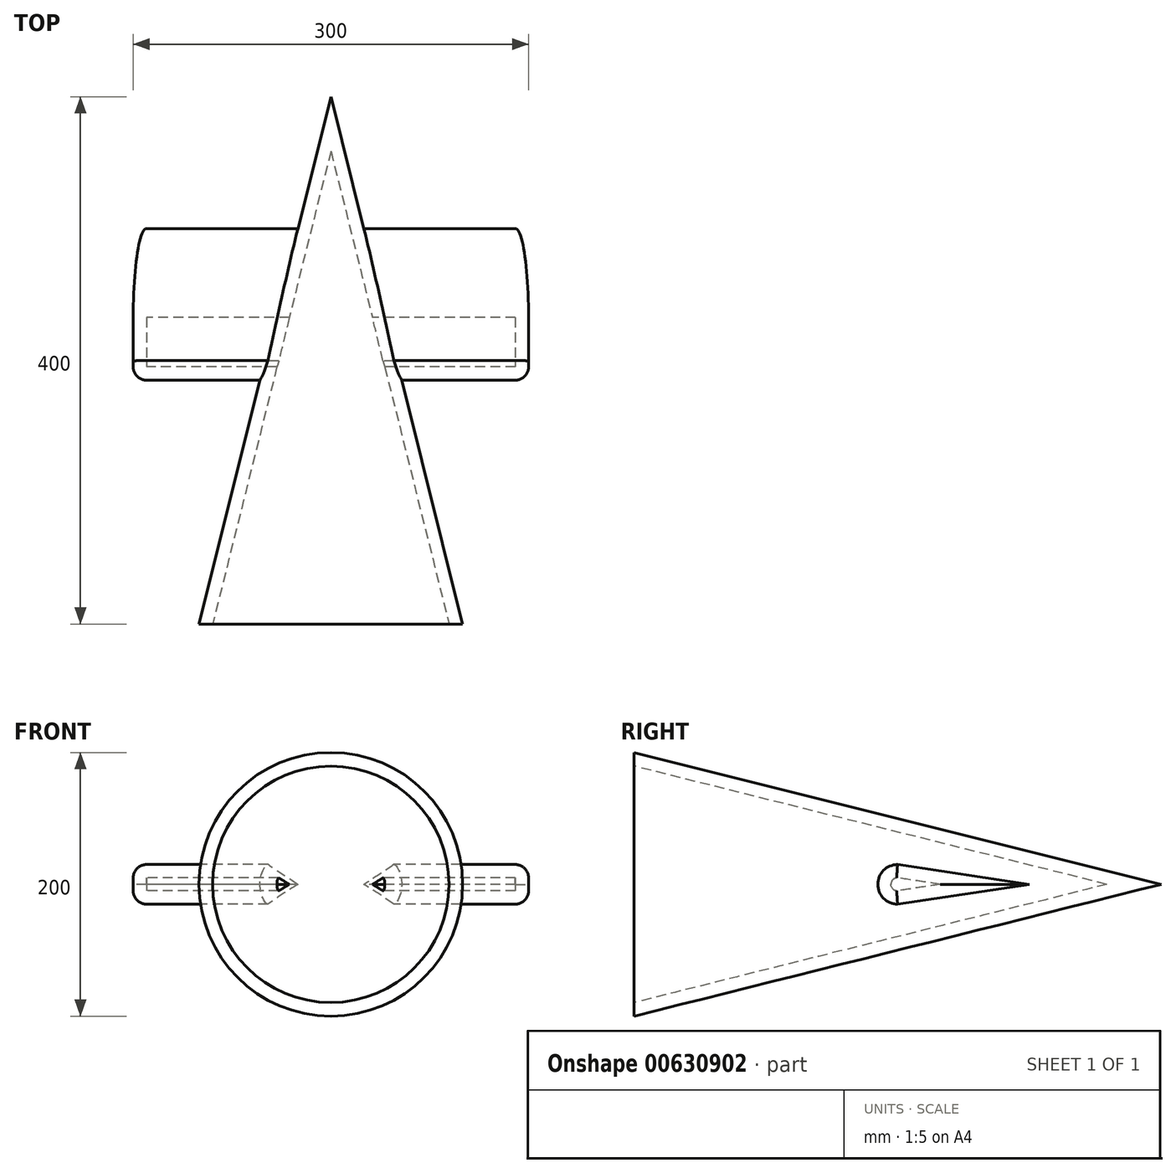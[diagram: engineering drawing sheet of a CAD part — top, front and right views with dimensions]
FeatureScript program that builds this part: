
annotation { "Feature Type Name" : "Feature", "Feature Type Description" : "" }
export const myFeature = defineFeature(function(context is Context, id is Id, definition is map)
    precondition{}
    {
        {
            var Q0;
            Q0=qCreatedBy(makeId("Right.planeOp"),FACE);
            var sketch = newSketch(context, id + "F0", { "sketchPlane" : qUnion([Q0])});
            skLineSegment(sketch, "E0", {"start": v(0, 0) * mm, "end": v(0, 100) * mm});
            skLineSegment(sketch, "E1", {"start": v(0, 0) * mm, "end": v(400, 0) * mm});
            skLineSegment(sketch, "E2", {"start": v(0, 100) * mm, "end": v(400, 0) * mm});
            skLineSegment(sketch, "E3", {"start": v(0, 0) * mm, "end": v(0, -100) * mm});
            skLineSegment(sketch, "E4", {"start": v(0, -100) * mm, "end": v(400, 0) * mm});
            skArc(sketch, "E5", {"start": v(200, 15) * mm, "mid": v(185, 0) * mm, "end": v(200, -15) * mm});
            skLineSegment(sketch, "E6", {"start": v(200, -15) * mm, "end": v(300, 0) * mm});
            skLineSegment(sketch, "E7", {"start": v(200, 15) * mm, "end": v(300, 0) * mm});
            skSolve(sketch);
        }
        {
            var Q0;
            {var subQ0=sQuery(id+"F0.wireOp",EDGE,"E7");Q0=makeQuery(id+"F0.imprint","IMPRINT",FACE,{"disambiguationData":[TD([[makeQuery(id+"F0.imprint","IMPRINT",EDGE,{"derivedFrom":subQ0}),-1.0]])]});}
            var Q1;
            {var subQ0=sQuery(id+"F0.wireOp",EDGE,"E6");Q1=makeQuery(id+"F0.imprint","IMPRINT",FACE,{"disambiguationData":[TD([[makeQuery(id+"F0.imprint","IMPRINT",EDGE,{"derivedFrom":subQ0}),1.0]])]});}
            extrude(context, id + "F1", {"entities" : qUnion([Q0, Q1]), "endBound" : BoundingType.SYMMETRIC, "depth" : 300 * mm, "offsetDistance" : 25 * mm});
        }
        {
            var Q0;
            {var subQ3=sQuery(id+"F0.wireOp",EDGE,"E0");Q0=makeQuery(id+"F0.imprint","IMPRINT",FACE,{"disambiguationData":[TD([[makeQuery(id+"F0.imprint","IMPRINT",EDGE,{"derivedFrom":subQ3}),-1.0]])]});}
            var Q1;
            Q1=sQuery(id+"F0.wireOp",EDGE,"E1");
            revolve(context, id + "F2", {"operationType" : NewBodyOperationType.ADD, "entities" : qUnion([Q0]), "axis" : qUnion([Q1]), "revolveType" : RevolveType.FULL});
        }
        {
            var Q0;
            Q0=makeQuery(id+"F1.opExtrude","CAP_FACE",FACE,{"disambiguationData":[OSD([sQuery(id+"F0.wireOp",EDGE,"E5"),sQuery(id+"F0.wireOp",EDGE,"E6"),sQuery(id+"F0.wireOp",EDGE,"E7")])],"isStart":false});
            var Q1;
            Q1=makeQuery(id+"F1.opExtrude","CAP_FACE",FACE,{"disambiguationData":[OSD([sQuery(id+"F0.wireOp",EDGE,"E5"),sQuery(id+"F0.wireOp",EDGE,"E6"),sQuery(id+"F0.wireOp",EDGE,"E7")])],"isStart":true});
            fillet(context, id + "F3", {"entities" : qUnion([Q0, Q1]), "radius" : 10 * mm, "tangentPropagation" : true, "allowEdgeOverflow" : false});
        }
        {
            var Q0;
            Q0=makeQuery(id+"F2.opRevolve","SWEPT_FACE",FACE,{"disambiguationData":[OSD([sQuery(id+"F0.wireOp",EDGE,"E0")])]});
            shell(context, id + "F4", {"entities" : qUnion([Q0]), "thickness" : 10 * mm});
        }
    });
